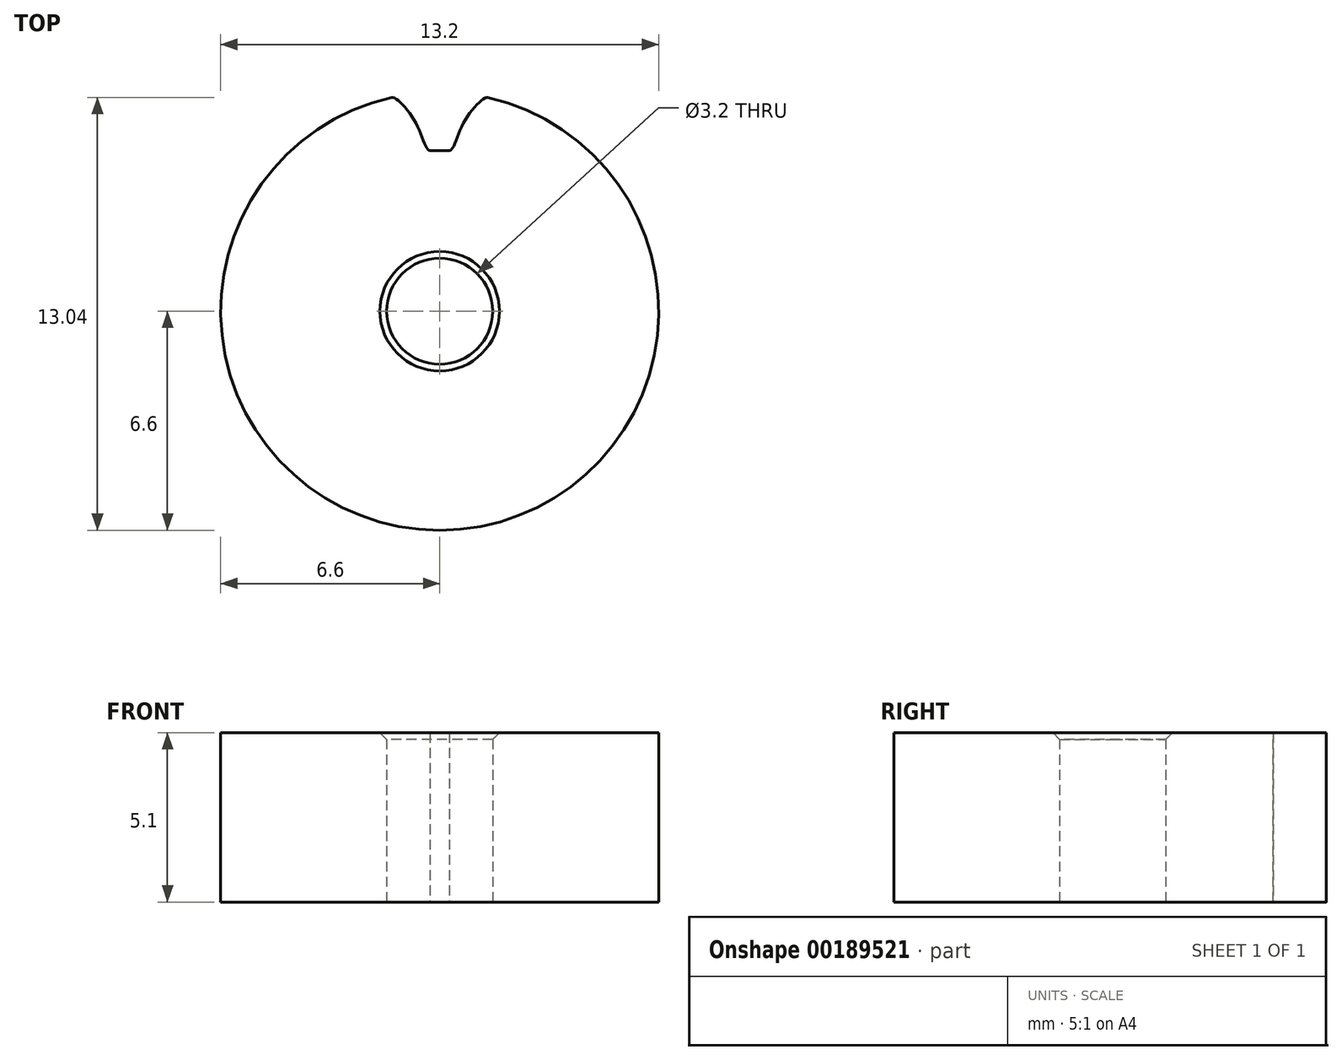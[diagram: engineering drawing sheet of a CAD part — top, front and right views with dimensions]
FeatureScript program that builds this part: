
annotation { "Feature Type Name" : "Feature", "Feature Type Description" : "" }
export const myFeature = defineFeature(function(context is Context, id is Id, definition is map)
    precondition{}
    {
        {
            var Q0;
            Q0=qCreatedBy(makeId("Top.planeOp"),FACE);
            var sketch = newSketch(context, id + "F0", { "sketchPlane" : qUnion([Q0])});
            skCircle(sketch, "E0", {"center": v(0, 0) * mm, "radius": 6.6 * mm});
            skCircle(sketch, "E1", {"center": v(0, 0) * mm, "radius": 4.85 * mm});
            skFitSpline(sketch, "E2", {"points": [v(-1.45, 6.44) * mm, v(-0.73, 5.7) * mm, v(-0.29, 4.84) * mm], "startDerivative": vector(0.74, 0.16) * mm, "endDerivative": vector(0.85, 0.06) * mm});
            skLineSegment(sketch, "E3", {"start": v(-0.29, 4.84) * mm, "end": v(0, 4.84) * mm});
            skLineSegment(sketch, "E4", {"start": v(-1.45, 6.44) * mm, "end": v(-1.45, 7.24) * mm});
            skLineSegment(sketch, "E5", {"start": v(-1.45, 7.24) * mm, "end": v(0, 7.24) * mm});
            skLineSegment(sketch, "E6.MirrorCS", {"start": v(1.45, 7.24) * mm, "end": v(0, 7.24) * mm});
            skLineSegment(sketch, "E7.MirrorCS", {"start": v(1.45, 6.44) * mm, "end": v(1.45, 7.24) * mm});
            skFitSpline(sketch, "E8.MirrorCS", {"points": [v(1.45, 6.44) * mm, v(0.73, 5.7) * mm, v(0.29, 4.84) * mm], "startDerivative": vector(-0.74, 0.16) * mm, "endDerivative": vector(-0.85, 0.06) * mm});
            skLineSegment(sketch, "E9.MirrorCS", {"start": v(0.29, 4.84) * mm, "end": v(0, 4.84) * mm});
            skSolve(sketch);
        }
        {
            var Q0;
            {var subQ0=sQuery(id+"F0.wireOp",EDGE,"E2");Q0=makeQuery(id+"F0.imprint","IMPRINT",FACE,{"disambiguationData":[TD([[makeQuery(id+"F0.imprint","IMPRINT",EDGE,{"derivedFrom":subQ0}),1.0]])]});}
            var Q1;
            {var subQ0=sQuery(id+"F0.wireOp",EDGE,"E2");Q1=makeQuery(id+"F0.imprint","IMPRINT",FACE,{"disambiguationData":[TD([[makeQuery(id+"F0.imprint","IMPRINT",EDGE,{"derivedFrom":subQ0}),-1.0]])]});}
            var Q2;
            {var subQ0=sQuery(id+"F0.wireOp",EDGE,"E3");Q2=makeQuery(id+"F0.imprint","IMPRINT",FACE,{"disambiguationData":[TD([[makeQuery(id+"F0.imprint","IMPRINT",EDGE,{"derivedFrom":subQ0}),-1.0]])]});}
            extrude(context, id + "F1", {"entities" : qUnion([Q0, Q1, Q2]), "depth" : 5.1 * mm});
        }
        {
            var Q0;
            {var subQ0=sQuery(id+"F0.wireOp",EDGE,"E2");Q0=makeQuery(id+"F0.imprint","IMPRINT",FACE,{"disambiguationData":[TD([[makeQuery(id+"F0.imprint","IMPRINT",EDGE,{"derivedFrom":subQ0}),1.0]])]});}
            var Q1;
            {var subQ0=sQuery(id+"F0.wireOp",EDGE,"E4");Q1=makeQuery(id+"F0.imprint","IMPRINT",FACE,{"disambiguationData":[TD([[makeQuery(id+"F0.imprint","IMPRINT",EDGE,{"derivedFrom":subQ0}),-1.0]])]});}
            extrude(context, id + "F2", {"entities" : qUnion([Q0, Q1]), "operationType" : NewBodyOperationType.REMOVE, "depth" : 5.1 * mm});
        }
        {
            var Q0;
            Q0=qCreatedBy(makeId("Top.planeOp"),FACE);
            var sketch = newSketch(context, id + "F3", { "sketchPlane" : qUnion([Q0])});
            skCircle(sketch, "E10", {"center": v(0, 0) * mm, "radius": 1.6 * mm});
            skSolve(sketch);
        }
        {
            var Q0;
            Q0=makeQuery(id+"F3.imprint","IMPRINT",FACE,{"disambiguationData":[TD([[makeQuery(id+"F3.imprint","IMPRINT",EDGE,{"derivedFrom":sQuery(id+"F3.wireOp",EDGE,"E10")}),1.0]])]});
            extrude(context, id + "F4", {"entities" : qUnion([Q0]), "operationType" : NewBodyOperationType.REMOVE, "depth" : 25 * mm});
        }
        {
            var Q0;
            Q0=makeQuery(id+"F4.boolean.opBoolean","COPY",EDGE,{"derivedFrom":makeQuery(id+"F4.opExtrude","CAP_EDGE",EDGE,{"disambiguationData":[OSD([sQuery(id+"F3.wireOp",EDGE,"E10")])],"isStart":true})});
            var Q1;
            Q1=makeQuery(id+"F4.boolean.opBoolean","INTERSECT",EDGE,{"derivedFrom":[makeQuery(id+"F1.opExtrude","CAP_FACE",FACE,{"disambiguationData":[OSD([sQuery(id+"F0.wireOp",EDGE,"E0"),sQuery(id+"F0.wireOp",EDGE,"E1"),sQuery(id+"F0.wireOp",EDGE,"E3"),sQuery(id+"F0.wireOp",EDGE,"E9.MirrorCS")])],"isStart":false}),makeQuery(id+"F4.opExtrude","SWEPT_FACE",FACE,{"disambiguationData":[OSD([sQuery(id+"F3.wireOp",EDGE,"E10")])]})]});
            chamfer(context, id + "F5", {"entities" : qUnion([Q0, Q1]), "width" : 0.2 * mm, "tangentPropagation" : true});
        }
    });
